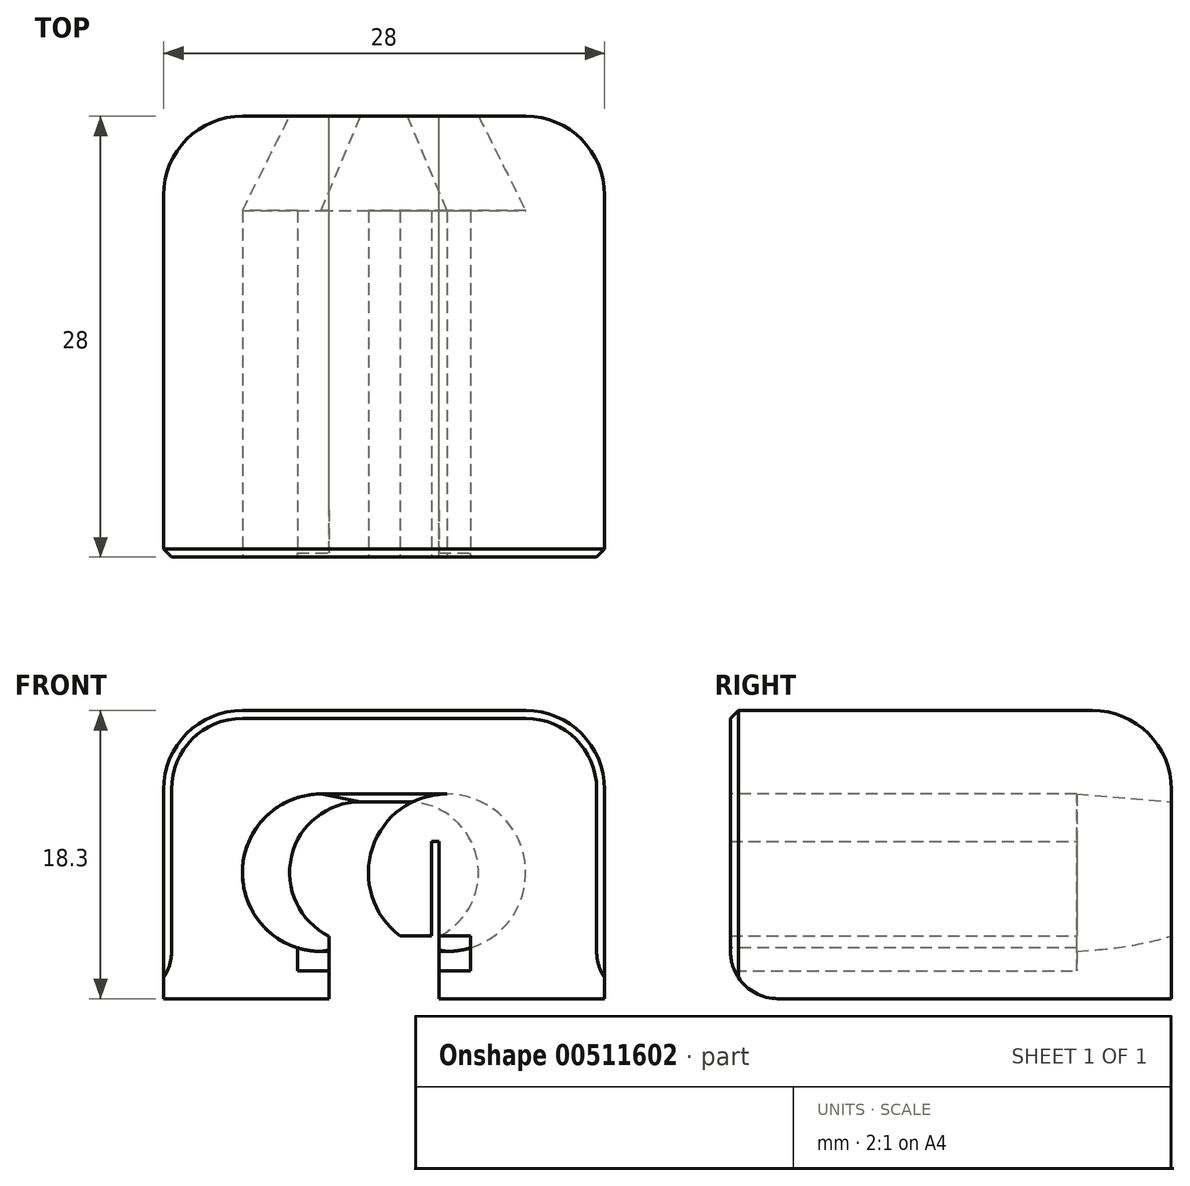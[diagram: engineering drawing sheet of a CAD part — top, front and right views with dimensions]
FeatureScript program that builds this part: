
annotation { "Feature Type Name" : "Feature", "Feature Type Description" : "" }
export const myFeature = defineFeature(function(context is Context, id is Id, definition is map)
    precondition{}
    {
        {
            var Q0;
            Q0=qCreatedBy(makeId("Top.planeOp"),FACE);
            var sketch = newSketch(context, id + "F0", { "sketchPlane" : qUnion([Q0])});
            skLineSegment(sketch, "E0.bottom", {"start": v(-14, -14) * mm, "end": v(14, -14) * mm});
            skLineSegment(sketch, "E0.top", {"start": v(-14, 14) * mm, "end": v(14, 14) * mm});
            skLineSegment(sketch, "E0.left", {"start": v(-14, -14) * mm, "end": v(-14, 14) * mm});
            skLineSegment(sketch, "E0.right", {"start": v(14, -14) * mm, "end": v(14, 14) * mm});
            skSolve(sketch);
        }
        {
            var Q0;
            Q0=makeQuery(id+"F0.imprint","IMPRINT",FACE,{"disambiguationData":[TD([[makeQuery(id+"F0.imprint","IMPRINT",EDGE,{"derivedFrom":sQuery(id+"F0.wireOp",EDGE,"E0.bottom")}),1.0]])]});
            extrude(context, id + "F1", {"entities" : qUnion([Q0]), "depth" : 18.3 * mm, "offsetDistance" : 25 * mm});
        }
        {
            var Q0;
            Q0=makeQuery(id+"F1.opExtrude","CAP_EDGE",EDGE,{"disambiguationData":[OSD([sQuery(id+"F0.wireOp",EDGE,"E0.left")])],"isStart":false});
            var Q1;
            Q1=makeQuery(id+"F1.opExtrude","CAP_EDGE",EDGE,{"disambiguationData":[OSD([sQuery(id+"F0.wireOp",EDGE,"E0.right")])],"isStart":false});
            var Q2;
            Q2=makeQuery(id+"F1.opExtrude","CAP_EDGE",EDGE,{"disambiguationData":[OSD([sQuery(id+"F0.wireOp",EDGE,"E0.top")])],"isStart":false});
            var Q3;
            Q3=makeQuery(id+"F1.opExtrude","SWEPT_EDGE",EDGE,{"disambiguationData":[OSD([sQuery(id+"F0.wireOp",EDGE,"E0.top"),sQuery(id+"F0.wireOp",EDGE,"E0.left")])]});
            var Q4;
            Q4=makeQuery(id+"F1.opExtrude","SWEPT_EDGE",EDGE,{"disambiguationData":[OSD([sQuery(id+"F0.wireOp",EDGE,"E0.top"),sQuery(id+"F0.wireOp",EDGE,"E0.right")])]});
            fillet(context, id + "F2", {"entities" : qUnion([Q0, Q1, Q2, Q3, Q4]), "tangentPropagation" : true, "radius" : 5 * mm, "defaultsChanged" : false, "vertexSettings" : [], "allowEdgeOverflow" : false});
        }
        {
            var Q0;
            Q0=makeQuery(id+"F1.opExtrude","SWEPT_FACE",FACE,{"disambiguationData":[OSD([sQuery(id+"F0.wireOp",EDGE,"E0.bottom")])]});
            var sketch = newSketch(context, id + "F3", { "sketchPlane" : qUnion([Q0])});
            skCircle(sketch, "E1", {"center": v(-4, 8) * mm, "radius": 5 * mm});
            skCircle(sketch, "E2", {"center": v(4, 8) * mm, "radius": 5 * mm});
            skLineSegment(sketch, "E3", {"start": v(-4, 13) * mm, "end": v(4, 13) * mm});
            skLineSegment(sketch, "E4", {"start": v(4, 3) * mm, "end": v(-4, 3) * mm});
            skLineSegment(sketch, "E5.bottom", {"start": v(-5.5, 1.75) * mm, "end": v(5.5, 1.75) * mm});
            skLineSegment(sketch, "E5.top", {"start": v(-5.5, 4) * mm, "end": v(5.5, 4) * mm});
            skLineSegment(sketch, "E5.left", {"start": v(-5.5, 1.75) * mm, "end": v(-5.5, 4) * mm});
            skLineSegment(sketch, "E5.right", {"start": v(5.5, 1.75) * mm, "end": v(5.5, 4) * mm});
            skLineSegment(sketch, "E6.bottom", {"start": v(-3, 1.75) * mm, "end": v(3, 1.75) * mm});
            skLineSegment(sketch, "E6.top", {"start": v(-3, 0) * mm, "end": v(3, 0) * mm});
            skLineSegment(sketch, "E6.left", {"start": v(-3, 1.75) * mm, "end": v(-3, 0) * mm});
            skLineSegment(sketch, "E6.right", {"start": v(3, 1.75) * mm, "end": v(3, 0) * mm});
            skSolve(sketch);
        }
        {
            var Q0;
            {var subQ0=sQuery(id+"F3.wireOp",EDGE,"E1");var subQ1=makeQuery(id+"F3.imprint","INTERSECT",VERTEX,{"derivedFrom":[subQ0,sQuery(id+"F3.wireOp",EDGE,"E3")]});Q0=makeQuery(id+"F3.imprint","IMPRINT",FACE,{"disambiguationData":[TD([[makeQuery(id+"F3.imprint","IMPRINT",EDGE,{"disambiguationData":[TD([[subQ1,1.0]])],"derivedFrom":subQ0}),1.0]])]});}
            var Q1;
            {var subQ2=sQuery(id+"F3.wireOp",EDGE,"E1");var subQ4=makeQuery(id+"F3.imprint","IMPRINT",VERTEX,{"derivedFrom":subQ2});Q1=makeQuery(id+"F3.imprint","IMPRINT",FACE,{"disambiguationData":[TD([[makeQuery(id+"F3.imprint","IMPRINT",EDGE,{"disambiguationData":[TD([[subQ4,-1.0]])],"derivedFrom":subQ2}),-1.0]])]});}
            var Q2;
            {var subQ0=sQuery(id+"F3.wireOp",EDGE,"E1");var subQ1=makeQuery(id+"F3.imprint","IMPRINT",VERTEX,{"derivedFrom":subQ0});Q2=makeQuery(id+"F3.imprint","IMPRINT",FACE,{"disambiguationData":[TD([[makeQuery(id+"F3.imprint","IMPRINT",EDGE,{"disambiguationData":[TD([[subQ1,-1.0]])],"derivedFrom":subQ0}),1.0]])]});}
            var Q3;
            {var subQ0=sQuery(id+"F3.wireOp",EDGE,"E3");Q3=makeQuery(id+"F3.imprint","IMPRINT",FACE,{"disambiguationData":[TD([[makeQuery(id+"F3.imprint","IMPRINT",EDGE,{"derivedFrom":subQ0}),-1.0]])]});}
            var Q4;
            {var subQ0=sQuery(id+"F3.wireOp",EDGE,"E4");Q4=makeQuery(id+"F3.imprint","IMPRINT",FACE,{"disambiguationData":[TD([[makeQuery(id+"F3.imprint","IMPRINT",EDGE,{"derivedFrom":subQ0}),-1.0]])]});}
            var Q5;
            Q5=makeQuery(id+"F3.imprint","IMPRINT",FACE,{"disambiguationData":[TD([[makeQuery(id+"F3.imprint","IMPRINT",EDGE,{"derivedFrom":sQuery(id+"F3.wireOp",EDGE,"E5.top")}),-1.0]])]});
            var Q6;
            Q6=makeQuery(id+"F3.imprint","IMPRINT",FACE,{"disambiguationData":[TD([[makeQuery(id+"F3.imprint","IMPRINT",EDGE,{"derivedFrom":sQuery(id+"F3.wireOp",EDGE,"E6.top")}),1.0]])]});
            var Q7;
            {var subQ0=sQuery(id+"F3.wireOp",EDGE,"E5.top");var subQ1=sQuery(id+"F3.wireOp",EDGE,"E1");var subQ2=makeQuery(id+"F3.imprint","INTERSECT",VERTEX,{"derivedFrom":[subQ1,subQ0]});Q7=makeQuery(id+"F3.imprint","IMPRINT",FACE,{"disambiguationData":[TD([[makeQuery(id+"F3.imprint","IMPRINT",EDGE,{"disambiguationData":[TD([[subQ2,-1.0]])],"derivedFrom":subQ1}),-1.0]])]});}
            extrude(context, id + "F4", {"entities" : qUnion([Q0, Q1, Q2, Q3, Q4, Q5, Q6, Q7]), "operationType" : NewBodyOperationType.REMOVE, "oppositeDirection" : true, "depth" : 22 * mm, "offsetDistance" : 25 * mm});
        }
        {
            var Q0;
            Q0=makeQuery(id+"F1.opExtrude","SWEPT_FACE",FACE,{"disambiguationData":[OSD([sQuery(id+"F0.wireOp",EDGE,"E0.top")])]});
            var sketch = newSketch(context, id + "F5", { "sketchPlane" : qUnion([Q0])});
            skArc(sketch, "E7", {"start": v(-1.5, 12.5) * mm, "mid": v(-6, 8) * mm, "end": v(-1.5, 3.5) * mm});
            skArc(sketch, "E8", {"start": v(1.5, 3.5) * mm, "mid": v(6, 8) * mm, "end": v(1.5, 12.5) * mm});
            skLineSegment(sketch, "E9", {"start": v(-1.5, 12.5) * mm, "end": v(1.5, 12.5) * mm});
            skLineSegment(sketch, "E10", {"start": v(1.5, 3.5) * mm, "end": v(-1.5, 3.5) * mm});
            skSolve(sketch);
        }
        {
            var Q0;
            Q0=makeQuery(id+"F4.boolean.opBoolean","COPY",FACE,{"derivedFrom":makeQuery(id+"F4.opExtrude","CAP_FACE",FACE,{"disambiguationData":[OSD([sQuery(id+"F3.wireOp",EDGE,"E1"),sQuery(id+"F3.wireOp",EDGE,"E2"),sQuery(id+"F3.wireOp",EDGE,"E3"),sQuery(id+"F3.wireOp",EDGE,"E4")])],"isStart":false})});
            var sketch = newSketch(context, id + "F6", { "sketchPlane" : qUnion([Q0])});
            skArc(sketch, "E11.0", {"start": v(-4, 13) * mm, "mid": v(-9, 8) * mm, "end": v(-4, 3) * mm});
            skLineSegment(sketch, "E11.1", {"start": v(4, 13) * mm, "end": v(-4, 13) * mm});
            skArc(sketch, "E11.2", {"start": v(4, 3) * mm, "mid": v(9, 8) * mm, "end": v(4, 13) * mm});
            skLineSegment(sketch, "E11.3", {"start": v(-4, 3) * mm, "end": v(4, 3) * mm});
            skSolve(sketch);
        }
        {
            var Q0;
            Q0 = qSketchRegion(id + "F6", true);
            var Q1;
            Q1 = qSketchRegion(id + "F5", true);
            loft(context, id + "F7", {"operationType" : NewBodyOperationType.REMOVE, "sheetProfilesArray" : [{ "sheetProfileEntities" : qUnion([Q0]) }, { "sheetProfileEntities" : qUnion([Q1]) }]});
        }
        {
            var Q0;
            {var subQ3=sQuery(id+"F3.wireOp",EDGE,"E4");Q0=makeQuery(id+"F3.imprint","IMPRINT",FACE,{"disambiguationData":[TD([[makeQuery(id+"F3.imprint","IMPRINT",EDGE,{"derivedFrom":subQ3}),1.0]])]});}
            extrude(context, id + "F8", {"entities" : qUnion([Q0]), "operationType" : NewBodyOperationType.REMOVE, "oppositeDirection" : true, "depth" : 22 * mm, "offsetDistance" : 25 * mm});
        }
        {
            var Q0;
            Q0=makeQuery(id+"F1.opExtrude","CAP_FACE",FACE,{"disambiguationData":[OSD([sQuery(id+"F0.wireOp",EDGE,"E0.bottom"),sQuery(id+"F0.wireOp",EDGE,"E0.top"),sQuery(id+"F0.wireOp",EDGE,"E0.left"),sQuery(id+"F0.wireOp",EDGE,"E0.right")])],"isStart":true});
            var sketch = newSketch(context, id + "F9", { "sketchPlane" : qUnion([Q0])});
            skLineSegment(sketch, "E12.bottom", {"start": v(-3.5, 14) * mm, "end": v(3.5, 14) * mm});
            skLineSegment(sketch, "E12.top", {"start": v(-3.5, -14) * mm, "end": v(3.5, -14) * mm});
            skLineSegment(sketch, "E12.left", {"start": v(-3.5, 14) * mm, "end": v(-3.5, -14) * mm});
            skLineSegment(sketch, "E12.right", {"start": v(3.5, 14) * mm, "end": v(3.5, -14) * mm});
            skSolve(sketch);
        }
        {
            var Q0;
            Q0=makeQuery(id+"F9.imprint","IMPRINT",FACE,{"disambiguationData":[TD([[makeQuery(id+"F9.imprint","IMPRINT",EDGE,{"derivedFrom":sQuery(id+"F9.wireOp",EDGE,"E12.top")}),1.0]])]});
            var Q1;
            {var subQ1=sQuery(id+"F3.wireOp",EDGE,"E6.top");Q1=makeQuery(id+"F9.imprint","IMPRINT",FACE,{"disambiguationData":[TD([[makeQuery(id+"F9.imprint","IMPRINT",EDGE,{"derivedFrom":makeQuery(id+"F4.boolean.opBoolean","COPY",EDGE,{"derivedFrom":makeQuery(id+"F4.opExtrude","CAP_EDGE",EDGE,{"disambiguationData":[OSD([subQ1])],"isStart":false})})}),1.0]])]});}
            extrude(context, id + "F10", {"entities" : qUnion([Q0, Q1]), "operationType" : NewBodyOperationType.REMOVE, "oppositeDirection" : true, "depth" : 10 * mm, "offsetDistance" : 25 * mm});
        }
        {
            var Q0;
            Q0=makeQuery(id+"F1.opExtrude","SWEPT_EDGE",EDGE,{"disambiguationData":[OSD([sQuery(id+"F0.wireOp",EDGE,"E0.bottom"),sQuery(id+"F0.wireOp",EDGE,"E0.left")])]});
            var Q1;
            Q1=makeQuery(id+"F4.boolean.opBoolean","COPY",EDGE,{"derivedFrom":makeQuery(id+"F4.opExtrude","CAP_EDGE",EDGE,{"disambiguationData":[OSD([sQuery(id+"F3.wireOp",EDGE,"E1")])],"isStart":true})});
            var Q2;
            Q2=makeQuery(id+"F8.boolean.opBoolean","COPY",EDGE,{"derivedFrom":makeQuery(id+"F8.opExtrude","CAP_EDGE",EDGE,{"disambiguationData":[OSD([sQuery(id+"F3.wireOp",EDGE,"E5.right")])],"isStart":true})});
            var Q3;
            Q3=makeQuery(id+"F8.boolean.opBoolean","COPY",EDGE,{"derivedFrom":makeQuery(id+"F8.opExtrude","CAP_EDGE",EDGE,{"disambiguationData":[OSD([sQuery(id+"F3.wireOp",EDGE,"E5.left")])],"isStart":true})});
            chamfer(context, id + "F11", {"entities" : qUnion([Q0, Q1, Q2, Q3]), "width" : 0.5 * mm, "tangentPropagation" : true});
        }
        {
            var Q0;
            {var subQ0=sQuery(id+"F0.wireOp",EDGE,"E0.bottom");var subQ1=sQuery(id+"F0.wireOp",EDGE,"E0.left");Q0=makeQuery(id+"F4.boolean.opBoolean","SPLIT",EDGE,{"disambiguationData":[TD([makeQuery(id+"F1.opExtrude","SWEPT_FACE",FACE,{"disambiguationData":[OSD([subQ1])]})])],"derivedFrom":makeQuery(id+"F1.opExtrude","CAP_EDGE",EDGE,{"disambiguationData":[OSD([subQ0])],"isStart":true})});}
            var Q1;
            {var subQ0=sQuery(id+"F0.wireOp",EDGE,"E0.bottom");var subQ1=sQuery(id+"F0.wireOp",EDGE,"E0.right");Q1=makeQuery(id+"F4.boolean.opBoolean","SPLIT",EDGE,{"disambiguationData":[TD([makeQuery(id+"F1.opExtrude","SWEPT_FACE",FACE,{"disambiguationData":[OSD([subQ1])]})])],"derivedFrom":makeQuery(id+"F1.opExtrude","CAP_EDGE",EDGE,{"disambiguationData":[OSD([subQ0])],"isStart":true})});}
            fillet(context, id + "F12", {"entities" : qUnion([Q0, Q1]), "tangentPropagation" : true, "radius" : 3 * mm, "defaultsChanged" : false, "vertexSettings" : [], "allowEdgeOverflow" : false});
        }
    });
